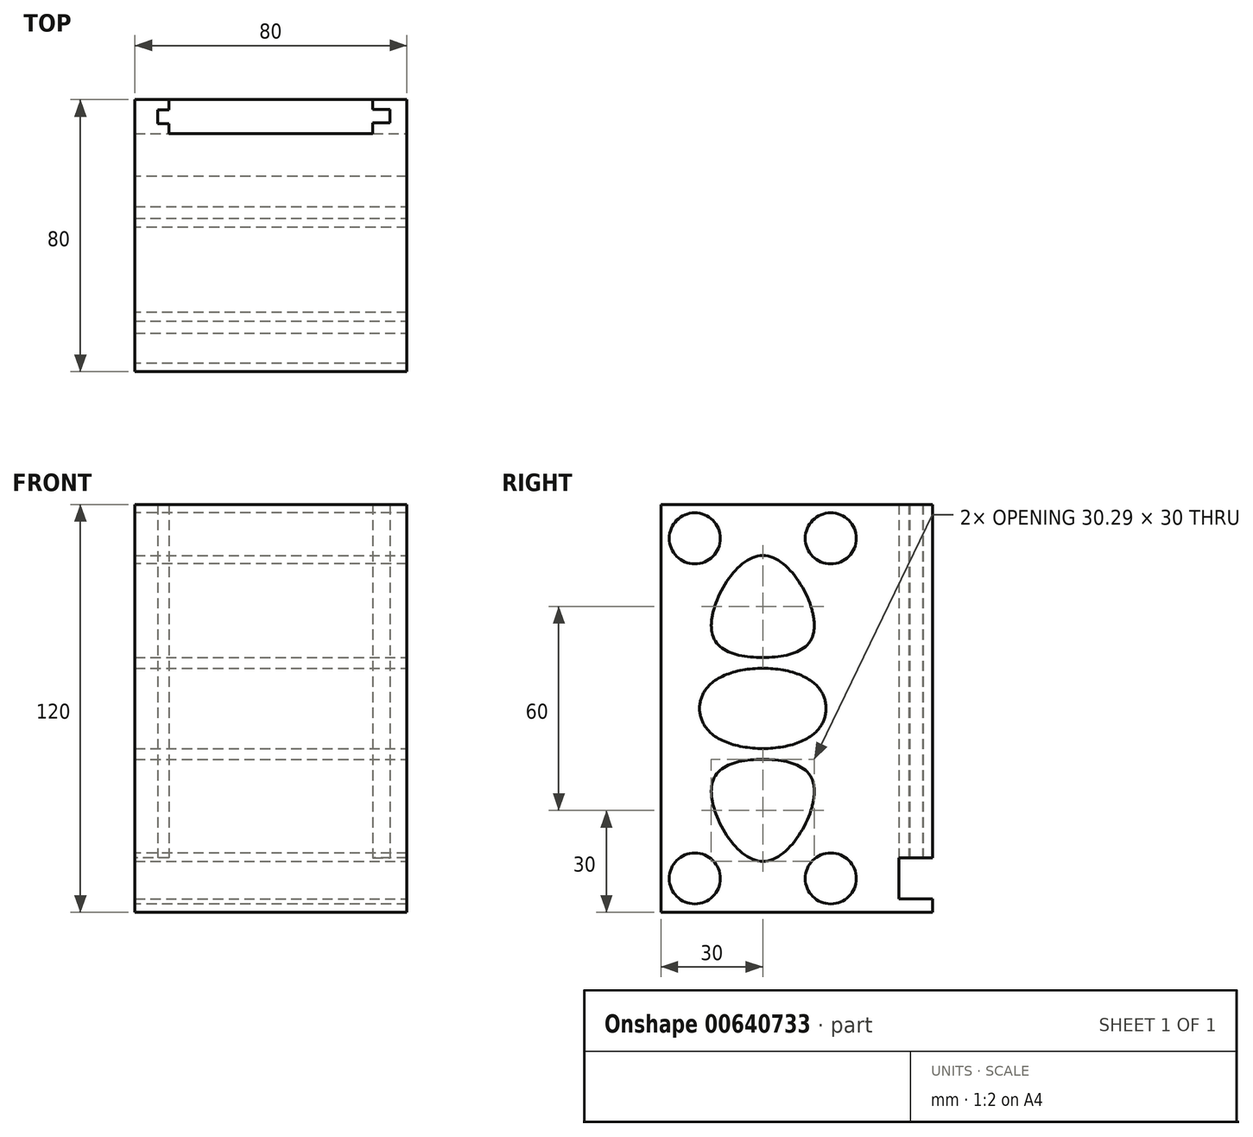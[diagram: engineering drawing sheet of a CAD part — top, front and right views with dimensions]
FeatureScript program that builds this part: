
annotation { "Feature Type Name" : "Feature", "Feature Type Description" : "" }
export const myFeature = defineFeature(function(context is Context, id is Id, definition is map)
    precondition{}
    {
        {
            var Q0;
            Q0=qCreatedBy(makeId("Top.planeOp"),FACE);
            var sketch = newSketch(context, id + "F0", { "sketchPlane" : qUnion([Q0])});
            skLineSegment(sketch, "E0.bottom", {"start": v(-25, 10) * mm, "end": v(25, 10) * mm});
            skLineSegment(sketch, "E0.top", {"start": v(-25, -10) * mm, "end": v(25, -10) * mm});
            skLineSegment(sketch, "E0.left", {"start": v(-25, 10) * mm, "end": v(-25, -10) * mm});
            skLineSegment(sketch, "E0.right", {"start": v(25, 10) * mm, "end": v(25, -10) * mm});
            skPoint(sketch, "E0.middle", {"position": v(0, 0) * mm});
            skPoint(sketch, "E1.middle", {"position": v(-25, 10) * mm});
            skPoint(sketch, "E2.middle", {"position": v(25, 10) * mm});
            skPoint(sketch, "E3.middle", {"position": v(25, -10) * mm});
            skLineSegment(sketch, "E4.bottom", {"start": v(-50, 0) * mm, "end": v(0, 0) * mm});
            skLineSegment(sketch, "E4.top", {"start": v(-50, -20) * mm, "end": v(0, -20) * mm});
            skLineSegment(sketch, "E4.left", {"start": v(-50, 0) * mm, "end": v(-50, -20) * mm});
            skLineSegment(sketch, "E4.right", {"start": v(0, 0) * mm, "end": v(0, -20) * mm});
            skPoint(sketch, "E4.middle", {"position": v(-25, -10) * mm});
            skLineSegment(sketch, "E5.bottom", {"start": v(0, 0) * mm, "end": v(50, 0) * mm});
            skLineSegment(sketch, "E5.top", {"start": v(0, -20) * mm, "end": v(50, -20) * mm});
            skLineSegment(sketch, "E5.right", {"start": v(50, 0) * mm, "end": v(50, -20) * mm});
            skLineSegment(sketch, "E6.bottom", {"start": v(50, 0) * mm, "end": v(0, 0) * mm});
            skLineSegment(sketch, "E6.top", {"start": v(50, 20) * mm, "end": v(0, 20) * mm});
            skLineSegment(sketch, "E6.left", {"start": v(50, 0) * mm, "end": v(50, 20) * mm});
            skLineSegment(sketch, "E6.right", {"start": v(0, 0) * mm, "end": v(0, 20) * mm});
            skLineSegment(sketch, "E7.top", {"start": v(-50, 20) * mm, "end": v(0, 20) * mm});
            skLineSegment(sketch, "E7.left", {"start": v(-50, 0) * mm, "end": v(-50, 20) * mm});
            skCircle(sketch, "E8", {"center": v(-50, 20) * mm, "radius": 10 * mm});
            skCircle(sketch, "E9", {"center": v(50, 20) * mm, "radius": 10 * mm});
            skCircle(sketch, "E10", {"center": v(50, -20) * mm, "radius": 10 * mm});
            skCircle(sketch, "E11", {"center": v(-50, -20) * mm, "radius": 10 * mm});
            skCircle(sketch, "E12", {"center": v(-50, 0) * mm, "radius": 10 * mm});
            skCircle(sketch, "E13", {"center": v(50, 0) * mm, "radius": 10 * mm});
            skLineSegment(sketch, "E14.bottom", {"start": v(-30, 30) * mm, "end": v(30, 30) * mm});
            skLineSegment(sketch, "E14.top", {"start": v(-30, 10) * mm, "end": v(30, 10) * mm});
            skLineSegment(sketch, "E14.left", {"start": v(-30, 30) * mm, "end": v(-30, 10) * mm});
            skLineSegment(sketch, "E14.right", {"start": v(30, 30) * mm, "end": v(30, 10) * mm});
            skPoint(sketch, "E14.middle", {"position": v(0, 20) * mm});
            skLineSegment(sketch, "E15", {"start": v(-30, 20) * mm, "end": v(-30, 10) * mm});
            skLineSegment(sketch, "E16.bottom", {"start": v(-33.31, 17) * mm, "end": v(-26.69, 17) * mm});
            skLineSegment(sketch, "E16.top", {"start": v(-33.31, 13) * mm, "end": v(-26.69, 13) * mm});
            skLineSegment(sketch, "E16.left", {"start": v(-33.31, 17) * mm, "end": v(-33.31, 13) * mm});
            skLineSegment(sketch, "E16.right", {"start": v(-26.69, 17) * mm, "end": v(-26.69, 13) * mm});
            skPoint(sketch, "E16.middle", {"position": v(-30, 15) * mm});
            skLineSegment(sketch, "E17.bottom", {"start": v(35, 17.2) * mm, "end": v(25, 17.2) * mm});
            skLineSegment(sketch, "E17.top", {"start": v(35, 13.2) * mm, "end": v(25, 13.2) * mm});
            skLineSegment(sketch, "E17.left", {"start": v(35, 17.2) * mm, "end": v(35, 13.2) * mm});
            skLineSegment(sketch, "E17.right", {"start": v(25, 17.2) * mm, "end": v(25, 13.2) * mm});
            skPoint(sketch, "E17.middle", {"position": v(30, 15.2) * mm});
            skFitSpline(sketch, "E18", {"points": [v(-40, -20) * mm, v(0, 0) * mm, v(40, -20) * mm], "startDerivative": vector(80, 60) * mm, "endDerivative": vector(80, -60) * mm});
            skSolve(sketch);
        }
        {
            var Q0;
            {var subQ0=sQuery(id+"F0.wireOp",EDGE,"E7.left");var subQ1=sQuery(id+"F0.wireOp",EDGE,"E7.top");var subQ2=makeQuery(id+"F0.imprint","INTERSECT",VERTEX,{"derivedFrom":[subQ1,subQ0]});Q0=makeQuery(id+"F0.imprint","IMPRINT",FACE,{"disambiguationData":[TD([[makeQuery(id+"F0.imprint","IMPRINT",EDGE,{"disambiguationData":[TD([[subQ2,-1.0]])],"derivedFrom":subQ1}),1.0]])]});}
            var Q1;
            {var subQ0=sQuery(id+"F0.wireOp",EDGE,"E7.left");var subQ1=sQuery(id+"F0.wireOp",EDGE,"E7.top");var subQ2=makeQuery(id+"F0.imprint","INTERSECT",VERTEX,{"derivedFrom":[subQ1,subQ0]});Q1=makeQuery(id+"F0.imprint","IMPRINT",FACE,{"disambiguationData":[TD([[makeQuery(id+"F0.imprint","IMPRINT",EDGE,{"disambiguationData":[TD([[subQ2,-1.0]])],"derivedFrom":subQ1}),-1.0]])]});}
            var Q2;
            {var subQ0=sQuery(id+"F0.wireOp",EDGE,"E16.left");Q2=makeQuery(id+"F0.imprint","IMPRINT",FACE,{"disambiguationData":[TD([[makeQuery(id+"F0.imprint","IMPRINT",EDGE,{"derivedFrom":subQ0}),-1.0]])]});}
            var Q3;
            {var subQ0=sQuery(id+"F0.wireOp",EDGE,"E14.top");var subQ1=sQuery(id+"F0.wireOp",EDGE,"E0.left");var subQ2=makeQuery(id+"F0.imprint","INTERSECT",VERTEX,{"derivedFrom":[subQ1,subQ0]});Q3=makeQuery(id+"F0.imprint","IMPRINT",FACE,{"disambiguationData":[TD([[makeQuery(id+"F0.imprint","IMPRINT",EDGE,{"disambiguationData":[TD([[subQ2,-1.0]])],"derivedFrom":subQ1}),1.0]])]});}
            var Q4;
            {var subQ0=sQuery(id+"F0.wireOp",EDGE,"E14.top");var subQ1=sQuery(id+"F0.wireOp",EDGE,"E0.right");var subQ2=makeQuery(id+"F0.imprint","INTERSECT",VERTEX,{"derivedFrom":[subQ1,subQ0]});Q4=makeQuery(id+"F0.imprint","IMPRINT",FACE,{"disambiguationData":[TD([[makeQuery(id+"F0.imprint","IMPRINT",EDGE,{"disambiguationData":[TD([[subQ2,-1.0]])],"derivedFrom":subQ1}),-1.0]])]});}
            var Q5;
            {var subQ0=sQuery(id+"F0.wireOp",EDGE,"E6.bottom");var subQ1=sQuery(id+"F0.wireOp",EDGE,"E0.right");var subQ2=makeQuery(id+"F0.imprint","INTERSECT",VERTEX,{"derivedFrom":[subQ1,subQ0]});Q5=makeQuery(id+"F0.imprint","IMPRINT",FACE,{"disambiguationData":[TD([[makeQuery(id+"F0.imprint","IMPRINT",EDGE,{"disambiguationData":[TD([[subQ2,-1.0]])],"derivedFrom":subQ1}),-1.0]])]});}
            var Q6;
            {var subQ0=sQuery(id+"F0.wireOp",EDGE,"E4.bottom");var subQ1=sQuery(id+"F0.wireOp",EDGE,"E0.left");var subQ2=makeQuery(id+"F0.imprint","INTERSECT",VERTEX,{"derivedFrom":[subQ1,subQ0]});Q6=makeQuery(id+"F0.imprint","IMPRINT",FACE,{"disambiguationData":[TD([[makeQuery(id+"F0.imprint","IMPRINT",EDGE,{"disambiguationData":[TD([[subQ2,-1.0]])],"derivedFrom":subQ1}),1.0]])]});}
            var Q7;
            {var subQ1=sQuery(id+"F0.wireOp",EDGE,"E4.bottom");var subQ7=sQuery(id+"F0.wireOp",EDGE,"E0.left");var subQ9=makeQuery(id+"F0.imprint","INTERSECT",VERTEX,{"derivedFrom":[subQ7,subQ1]});Q7=makeQuery(id+"F0.imprint","IMPRINT",FACE,{"disambiguationData":[TD([[makeQuery(id+"F0.imprint","IMPRINT",EDGE,{"disambiguationData":[TD([[subQ9,-1.0]])],"derivedFrom":subQ7}),-1.0]])]});}
            var Q8;
            {var subQ0=sQuery(id+"F0.wireOp",EDGE,"E4.left");var subQ1=sQuery(id+"F0.wireOp",EDGE,"E4.top");var subQ2=makeQuery(id+"F0.imprint","INTERSECT",VERTEX,{"derivedFrom":[subQ1,subQ0]});Q8=makeQuery(id+"F0.imprint","IMPRINT",FACE,{"disambiguationData":[TD([[makeQuery(id+"F0.imprint","IMPRINT",EDGE,{"disambiguationData":[TD([[subQ2,-1.0]])],"derivedFrom":subQ1}),1.0]])]});}
            var Q9;
            {var subQ0=sQuery(id+"F0.wireOp",EDGE,"E4.left");var subQ1=sQuery(id+"F0.wireOp",EDGE,"E4.top");var subQ2=makeQuery(id+"F0.imprint","INTERSECT",VERTEX,{"derivedFrom":[subQ1,subQ0]});Q9=makeQuery(id+"F0.imprint","IMPRINT",FACE,{"disambiguationData":[TD([[makeQuery(id+"F0.imprint","IMPRINT",EDGE,{"disambiguationData":[TD([[subQ2,-1.0]])],"derivedFrom":subQ1}),-1.0]])]});}
            var Q10;
            {var subQ11=sQuery(id+"F0.wireOp",EDGE,"E17.left");Q10=makeQuery(id+"F0.imprint","IMPRINT",FACE,{"disambiguationData":[TD([[makeQuery(id+"F0.imprint","IMPRINT",EDGE,{"derivedFrom":subQ11}),1.0]])]});}
            var Q11;
            {var subQ0=sQuery(id+"F0.wireOp",EDGE,"E6.left");var subQ1=sQuery(id+"F0.wireOp",EDGE,"E6.top");var subQ2=makeQuery(id+"F0.imprint","INTERSECT",VERTEX,{"derivedFrom":[subQ1,subQ0]});Q11=makeQuery(id+"F0.imprint","IMPRINT",FACE,{"disambiguationData":[TD([[makeQuery(id+"F0.imprint","IMPRINT",EDGE,{"disambiguationData":[TD([[subQ2,-1.0]])],"derivedFrom":subQ1}),1.0]])]});}
            var Q12;
            {var subQ0=sQuery(id+"F0.wireOp",EDGE,"E6.left");var subQ1=sQuery(id+"F0.wireOp",EDGE,"E6.top");var subQ2=makeQuery(id+"F0.imprint","INTERSECT",VERTEX,{"derivedFrom":[subQ1,subQ0]});Q12=makeQuery(id+"F0.imprint","IMPRINT",FACE,{"disambiguationData":[TD([[makeQuery(id+"F0.imprint","IMPRINT",EDGE,{"disambiguationData":[TD([[subQ2,-1.0]])],"derivedFrom":subQ1}),-1.0]])]});}
            var Q13;
            {var subQ1=sQuery(id+"F0.wireOp",EDGE,"E6.bottom");var subQ7=sQuery(id+"F0.wireOp",EDGE,"E0.right");var subQ8=makeQuery(id+"F0.imprint","INTERSECT",VERTEX,{"derivedFrom":[subQ7,subQ1]});Q13=makeQuery(id+"F0.imprint","IMPRINT",FACE,{"disambiguationData":[TD([[makeQuery(id+"F0.imprint","IMPRINT",EDGE,{"disambiguationData":[TD([[subQ8,-1.0]])],"derivedFrom":subQ7}),1.0]])]});}
            var Q14;
            {var subQ0=sQuery(id+"F0.wireOp",EDGE,"E5.right");var subQ1=sQuery(id+"F0.wireOp",EDGE,"E5.top");var subQ2=makeQuery(id+"F0.imprint","INTERSECT",VERTEX,{"derivedFrom":[subQ1,subQ0]});Q14=makeQuery(id+"F0.imprint","IMPRINT",FACE,{"disambiguationData":[TD([[makeQuery(id+"F0.imprint","IMPRINT",EDGE,{"disambiguationData":[TD([[subQ2,1.0]])],"derivedFrom":subQ1}),1.0]])]});}
            var Q15;
            {var subQ0=sQuery(id+"F0.wireOp",EDGE,"E5.right");var subQ1=sQuery(id+"F0.wireOp",EDGE,"E5.top");var subQ2=makeQuery(id+"F0.imprint","INTERSECT",VERTEX,{"derivedFrom":[subQ1,subQ0]});Q15=makeQuery(id+"F0.imprint","IMPRINT",FACE,{"disambiguationData":[TD([[makeQuery(id+"F0.imprint","IMPRINT",EDGE,{"disambiguationData":[TD([[subQ2,1.0]])],"derivedFrom":subQ1}),-1.0]])]});}
            var Q16;
            {var subQ3=sQuery(id+"F0.wireOp",EDGE,"E0.top");var subQ7=sQuery(id+"F0.wireOp",EDGE,"E0.right");var subQ8=makeQuery(id+"F0.imprint","INTERSECT",VERTEX,{"derivedFrom":[subQ3,subQ7]});Q16=makeQuery(id+"F0.imprint","IMPRINT",FACE,{"disambiguationData":[TD([[makeQuery(id+"F0.imprint","IMPRINT",EDGE,{"disambiguationData":[TD([[subQ8,1.0]])],"derivedFrom":subQ3}),-1.0]])]});}
            var Q17;
            {var subQ5=sQuery(id+"F0.wireOp",EDGE,"E0.left");var subQ7=sQuery(id+"F0.wireOp",EDGE,"E0.top");var subQ8=makeQuery(id+"F0.imprint","INTERSECT",VERTEX,{"derivedFrom":[subQ7,subQ5]});Q17=makeQuery(id+"F0.imprint","IMPRINT",FACE,{"disambiguationData":[TD([[makeQuery(id+"F0.imprint","IMPRINT",EDGE,{"disambiguationData":[TD([[subQ8,-1.0]])],"derivedFrom":subQ7}),-1.0]])]});}
            var Q18;
            {var subQ0=sQuery(id+"F0.wireOp",EDGE,"E0.left");var subQ1=sQuery(id+"F0.wireOp",EDGE,"E0.top");var subQ2=makeQuery(id+"F0.imprint","INTERSECT",VERTEX,{"derivedFrom":[subQ1,subQ0]});Q18=makeQuery(id+"F0.imprint","IMPRINT",FACE,{"disambiguationData":[TD([[makeQuery(id+"F0.imprint","IMPRINT",EDGE,{"disambiguationData":[TD([[subQ2,-1.0]])],"derivedFrom":subQ1}),1.0]])]});}
            var Q19;
            {var subQ0=sQuery(id+"F0.wireOp",EDGE,"E0.right");var subQ1=sQuery(id+"F0.wireOp",EDGE,"E0.top");var subQ2=makeQuery(id+"F0.imprint","INTERSECT",VERTEX,{"derivedFrom":[subQ1,subQ0]});Q19=makeQuery(id+"F0.imprint","IMPRINT",FACE,{"disambiguationData":[TD([[makeQuery(id+"F0.imprint","IMPRINT",EDGE,{"disambiguationData":[TD([[subQ2,1.0]])],"derivedFrom":subQ1}),1.0]])]});}
            extrude(context, id + "F1", {"entities" : qUnion([Q0, Q1, Q2, Q3, Q4, Q5, Q6, Q7, Q8, Q9, Q10, Q11, Q12, Q13, Q14, Q15, Q16, Q17, Q18, Q19]), "depth" : 120 * mm, "offsetDistance" : 25 * mm});
        }
        {
            var Q0;
            {var subQ6=sQuery(id+"F0.wireOp",EDGE,"E16.right");Q0=makeQuery(id+"F0.imprint","IMPRINT",FACE,{"disambiguationData":[TD([[makeQuery(id+"F0.imprint","IMPRINT",EDGE,{"derivedFrom":subQ6}),1.0]])]});}
            var Q1;
            {var subQ5=sQuery(id+"F0.wireOp",EDGE,"E16.right");Q1=makeQuery(id+"F0.imprint","IMPRINT",FACE,{"disambiguationData":[TD([[makeQuery(id+"F0.imprint","IMPRINT",EDGE,{"derivedFrom":subQ5}),-1.0]])]});}
            var Q2;
            {var subQ5=sQuery(id+"F0.wireOp",EDGE,"E16.left");Q2=makeQuery(id+"F0.imprint","IMPRINT",FACE,{"disambiguationData":[TD([[makeQuery(id+"F0.imprint","IMPRINT",EDGE,{"derivedFrom":subQ5}),1.0]])]});}
            var Q3;
            {var subQ5=sQuery(id+"F0.wireOp",EDGE,"E17.left");Q3=makeQuery(id+"F0.imprint","IMPRINT",FACE,{"disambiguationData":[TD([[makeQuery(id+"F0.imprint","IMPRINT",EDGE,{"derivedFrom":subQ5}),-1.0]])]});}
            var Q4;
            {var subQ5=sQuery(id+"F0.wireOp",EDGE,"E17.right");Q4=makeQuery(id+"F0.imprint","IMPRINT",FACE,{"disambiguationData":[TD([[makeQuery(id+"F0.imprint","IMPRINT",EDGE,{"derivedFrom":subQ5}),1.0]])]});}
            var Q5;
            {var subQ13=sQuery(id+"F0.wireOp",EDGE,"E17.right");Q5=makeQuery(id+"F0.imprint","IMPRINT",FACE,{"disambiguationData":[TD([[makeQuery(id+"F0.imprint","IMPRINT",EDGE,{"derivedFrom":subQ13}),-1.0]])]});}
            extrude(context, id + "F2", {"entities" : qUnion([Q0, Q1, Q2, Q3, Q4, Q5]), "operationType" : NewBodyOperationType.ADD, "depth" : 4 * mm, "offsetDistance" : 25 * mm});
        }
        {
            var Q0;
            Q0=qCreatedBy(makeId("Right.planeOp"),FACE);
            var sketch = newSketch(context, id + "F3", { "sketchPlane" : qUnion([Q0])});
            skLineSegment(sketch, "E19", {"start": v(0, 0) * mm, "end": v(15, 0) * mm});
            skLineSegment(sketch, "E20", {"start": v(15, 0) * mm, "end": v(15, 10) * mm});
            skLineSegment(sketch, "E21.bottom", {"start": v(20, 16) * mm, "end": v(10, 16) * mm});
            skLineSegment(sketch, "E21.top", {"start": v(20, 4) * mm, "end": v(10, 4) * mm});
            skLineSegment(sketch, "E21.right", {"start": v(10, 16) * mm, "end": v(10, 4) * mm});
            skPoint(sketch, "E21.middle", {"position": v(15, 10) * mm});
            skLineSegment(sketch, "E22", {"start": v(20, 16) * mm, "end": v(30, 16) * mm});
            skLineSegment(sketch, "E23", {"start": v(20, 4) * mm, "end": v(30, 4) * mm});
            skLineSegment(sketch, "E24", {"start": v(30, 16) * mm, "end": v(30, 4) * mm});
            skSolve(sketch);
        }
        {
            var Q0;
            Q0=makeQuery(id+"F3.imprint","IMPRINT",FACE,{"disambiguationData":[TD([[makeQuery(id+"F3.imprint","IMPRINT",EDGE,{"derivedFrom":sQuery(id+"F3.wireOp",EDGE,"E21.bottom")}),1.0]])]});
            extrude(context, id + "F4", {"entities" : qUnion([Q0]), "operationType" : NewBodyOperationType.REMOVE, "depth" : 100 * mm, "offsetDistance" : 25 * mm, "hasSecondDirection" : true, "secondDirectionOppositeDirection" : true, "secondDirectionDepth" : 100 * mm});
        }
        {
            var Q0;
            Q0=qCreatedBy(makeId("Top.planeOp"),FACE);
            var sketch = newSketch(context, id + "F5", { "sketchPlane" : qUnion([Q0])});
            skLineSegment(sketch, "E25", {"start": v(0, 0) * mm, "end": v(-50, 0) * mm});
            skLineSegment(sketch, "E26", {"start": v(0, 0) * mm, "end": v(50, 0) * mm});
            skLineSegment(sketch, "E27.bottom", {"start": v(-60, -41.73) * mm, "end": v(-40, -41.73) * mm});
            skLineSegment(sketch, "E27.top", {"start": v(-60, 41.73) * mm, "end": v(-40, 41.73) * mm});
            skLineSegment(sketch, "E27.left", {"start": v(-60, -41.73) * mm, "end": v(-60, 41.73) * mm});
            skLineSegment(sketch, "E27.right", {"start": v(-40, -41.73) * mm, "end": v(-40, 41.73) * mm});
            skPoint(sketch, "E27.middle", {"position": v(-50, 0) * mm});
            skLineSegment(sketch, "E28.bottom", {"start": v(40, -36.42) * mm, "end": v(60, -36.42) * mm});
            skLineSegment(sketch, "E28.top", {"start": v(40, 36.42) * mm, "end": v(60, 36.42) * mm});
            skLineSegment(sketch, "E28.left", {"start": v(40, -36.42) * mm, "end": v(40, 36.42) * mm});
            skLineSegment(sketch, "E28.right", {"start": v(60, -36.42) * mm, "end": v(60, 36.42) * mm});
            skPoint(sketch, "E28.middle", {"position": v(50, 0) * mm});
            skSolve(sketch);
        }
        {
            var Q0;
            {var subQ1=sQuery(id+"F5.wireOp",EDGE,"E27.bottom");Q0=makeQuery(id+"F5.imprint","IMPRINT",FACE,{"disambiguationData":[TD([[makeQuery(id+"F5.imprint","IMPRINT",EDGE,{"derivedFrom":subQ1}),1.0]])]});}
            var Q1;
            {var subQ3=sQuery(id+"F5.wireOp",EDGE,"E28.bottom");Q1=makeQuery(id+"F5.imprint","IMPRINT",FACE,{"disambiguationData":[TD([[makeQuery(id+"F5.imprint","IMPRINT",EDGE,{"derivedFrom":subQ3}),1.0]])]});}
            extrude(context, id + "F6", {"entities" : qUnion([Q0, Q1]), "operationType" : NewBodyOperationType.REMOVE, "depth" : 120 * mm, "offsetDistance" : 25 * mm});
        }
        {
            var Q0;
            Q0=makeQuery(id+"F1.opExtrude","SWEPT_FACE",FACE,{"disambiguationData":[OSD([sQuery(id+"F0.wireOp",EDGE,"E4.top"),sQuery(id+"F0.wireOp",EDGE,"E5.top")])]});
            extrude(context, id + "F7", {"entities" : qUnion([Q0]), "operationType" : NewBodyOperationType.ADD, "depth" : 40 * mm, "offsetDistance" : 25 * mm});
        }
        {
            var Q0;
            Q0=qCreatedBy(makeId("Right.planeOp"),FACE);
            var sketch = newSketch(context, id + "F8", { "sketchPlane" : qUnion([Q0])});
            skLineSegment(sketch, "E29.bottom", {"start": v(0, 0) * mm, "end": v(-60, 0) * mm});
            skLineSegment(sketch, "E29.top", {"start": v(0, 120) * mm, "end": v(-60, 120) * mm});
            skLineSegment(sketch, "E29.left", {"start": v(0, 0) * mm, "end": v(0, 60) * mm});
            skLineSegment(sketch, "E29.right", {"start": v(-60, 0) * mm, "end": v(-60, 120) * mm});
            skLineSegment(sketch, "E30", {"start": v(-10, 60) * mm, "end": v(-30, 60) * mm});
            skLineSegment(sketch, "E31", {"start": v(-30, 110) * mm, "end": v(-30, 120) * mm});
            skLineSegment(sketch, "E32.bottom", {"start": v(-30, 110) * mm, "end": v(-42.5, 110) * mm});
            skLineSegment(sketch, "E32.top", {"start": v(-10, 10) * mm, "end": v(-50, 10) * mm});
            skLineSegment(sketch, "E32.left", {"start": v(-10, 110) * mm, "end": v(-10, 17.5) * mm});
            skLineSegment(sketch, "E32.right", {"start": v(-50, 110) * mm, "end": v(-50, 17.5) * mm});
            skPoint(sketch, "E32.middle", {"position": v(-30, 60) * mm});
            skCircle(sketch, "E33", {"center": v(-10, 110) * mm, "radius": 7.5 * mm});
            skCircle(sketch, "E34", {"center": v(-50, 110) * mm, "radius": 7.5 * mm});
            skCircle(sketch, "E35", {"center": v(-50, 10) * mm, "radius": 7.5 * mm});
            skCircle(sketch, "E36", {"center": v(-10, 10) * mm, "radius": 7.5 * mm});
            skPoint(sketch, "E37.start.orphan", {"position": v(-30, 0) * mm});
            skPoint(sketch, "E38.orphan", {"position": v(0, 60) * mm});
            skPoint(sketch, "E39.trimOffspring.end.orphan", {"position": v(-60, 60) * mm});
            skSolve(sketch);
        }
        {
            var Q0;
            Q0 = qSketchRegion(id + "F8", true);
            extrude(context, id + "F9", {"entities" : qUnion([Q0]), "operationType" : NewBodyOperationType.REMOVE, "depth" : 100 * mm, "offsetDistance" : 25 * mm, "hasSecondDirection" : true, "secondDirectionOppositeDirection" : true, "secondDirectionDepth" : 100 * mm});
        }
        {
            var Q0;
            Q0=qCreatedBy(makeId("Right.planeOp"),FACE);
            cPlane(context, id + "F10", {"entities" : qUnion([Q0]), "cplaneType" : CPlaneType.OFFSET, "offset" : 40 * mm, "width" : 150 * mm, "height" : 150 * mm});
        }
        {
            var Q0;
            Q0=qCreatedBy(id+"F10.planeOp",FACE);
            var sketch = newSketch(context, id + "F11", { "sketchPlane" : qUnion([Q0])});
            skLineSegment(sketch, "E40", {"start": v(0, 0) * mm, "end": v(0, 120) * mm});
            skLineSegment(sketch, "E41", {"start": v(0, 60) * mm, "end": v(-60, 60) * mm});
            skLineSegment(sketch, "E42", {"start": v(-60, 60) * mm, "end": v(-60, 120) * mm});
            skLineSegment(sketch, "E43", {"start": v(-60, 60) * mm, "end": v(-60, 0) * mm});
            skLineSegment(sketch, "E44", {"start": v(-60, 90) * mm, "end": v(0, 90) * mm});
            skLineSegment(sketch, "E45", {"start": v(-60, 30) * mm, "end": v(0, 30) * mm});
            skLineSegment(sketch, "E46", {"start": v(-30, 30) * mm, "end": v(-30, 60) * mm});
            skLineSegment(sketch, "E47", {"start": v(-30, 60) * mm, "end": v(-30, 90) * mm});
            skLineSegment(sketch, "E48", {"start": v(-60, 120) * mm, "end": v(-60, 90) * mm});
            skLineSegment(sketch, "E49", {"start": v(-60, 90) * mm, "end": v(-60, 60) * mm});
            skLineSegment(sketch, "E50", {"start": v(-60, 60) * mm, "end": v(-60, 30) * mm});
            skLineSegment(sketch, "E51", {"start": v(-60, 30) * mm, "end": v(-60, 0) * mm});
            skLineSegment(sketch, "E52", {"start": v(-60, 75) * mm, "end": v(0, 75) * mm});
            skLineSegment(sketch, "E53", {"start": v(0, 75) * mm, "end": v(-30, 60) * mm});
            skLineSegment(sketch, "E54", {"start": v(-60, 75) * mm, "end": v(-30, 60) * mm});
            skLineSegment(sketch, "E55", {"start": v(-60, 45) * mm, "end": v(0, 45) * mm});
            skLineSegment(sketch, "E56", {"start": v(0, 45) * mm, "end": v(-30, 60) * mm});
            skLineSegment(sketch, "E57", {"start": v(-60, 45) * mm, "end": v(-30, 60) * mm});
            skLineSegment(sketch, "E58", {"start": v(-60, 45) * mm, "end": v(-30, 30) * mm});
            skLineSegment(sketch, "E59", {"start": v(0, 45) * mm, "end": v(-30, 30) * mm});
            skLineSegment(sketch, "E60", {"start": v(-60, 75) * mm, "end": v(-30, 90) * mm});
            skLineSegment(sketch, "E61", {"start": v(0, 75) * mm, "end": v(-30, 90) * mm});
            skLineSegment(sketch, "E62", {"start": v(-60, 120) * mm, "end": v(0, 120) * mm});
            skLineSegment(sketch, "E63", {"start": v(-60, 90) * mm, "end": v(-30, 120) * mm});
            skLineSegment(sketch, "E64", {"start": v(-30, 120) * mm, "end": v(0, 90) * mm});
            skLineSegment(sketch, "E65", {"start": v(-60, 0) * mm, "end": v(0, 0) * mm});
            skLineSegment(sketch, "E66", {"start": v(-60, 30) * mm, "end": v(-30, 0) * mm});
            skLineSegment(sketch, "E67", {"start": v(-30, 0) * mm, "end": v(0, 30) * mm});
            skLineSegment(sketch, "E68", {"start": v(-30, 30) * mm, "end": v(-30, 0) * mm});
            skLineSegment(sketch, "E69", {"start": v(-30, 90) * mm, "end": v(-30, 120) * mm});
            skLineSegment(sketch, "E70", {"start": v(-162.58, 48.52) * mm, "end": v(-145.65, 65.46) * mm});
            skFitSpline(sketch, "E71", {"points": [v(-45, 37.5) * mm, v(-30, 15) * mm, v(-15, 37.5) * mm, v(-30, 45) * mm, v(-45, 37.5) * mm]});
            skFitSpline(sketch, "E72", {"points": [v(-45, 82.5) * mm, v(-30, 105) * mm, v(-15, 82.5) * mm, v(-30, 75) * mm, v(-45, 82.5) * mm]});
            skFitSpline(sketch, "E73", {"points": [v(-15, 52.5) * mm, v(-15, 67.5) * mm, v(-45, 67.5) * mm, v(-45, 52.5) * mm, v(-15, 52.5) * mm]});
            skSolve(sketch);
        }
        {
            var Q0;
            {var subQ1=sQuery(id+"F11.wireOp",EDGE,"E44");var subQ3=sQuery(id+"F11.wireOp",EDGE,"E72");var subQ4=makeQuery(id+"F11.imprint","INTERSECT",VERTEX,{"disambiguationData":[OD(0.0)],"derivedFrom":[subQ1,subQ3]});Q0=makeQuery(id+"F11.imprint","IMPRINT",FACE,{"disambiguationData":[TD([[makeQuery(id+"F11.imprint","IMPRINT",EDGE,{"disambiguationData":[TD([[subQ4,-1.0]])],"derivedFrom":subQ3}),-1.0]])]});}
            var Q1;
            {var subQ1=sQuery(id+"F11.wireOp",EDGE,"E44");var subQ3=sQuery(id+"F11.wireOp",EDGE,"E72");var subQ4=makeQuery(id+"F11.imprint","INTERSECT",VERTEX,{"disambiguationData":[OD(0.0)],"derivedFrom":[subQ1,subQ3]});Q1=makeQuery(id+"F11.imprint","IMPRINT",FACE,{"disambiguationData":[TD([[makeQuery(id+"F11.imprint","IMPRINT",EDGE,{"disambiguationData":[TD([[subQ4,1.0]])],"derivedFrom":subQ3}),-1.0]])]});}
            var Q2;
            {var subQ0=sQuery(id+"F11.wireOp",EDGE,"E60");var subQ3=sQuery(id+"F11.wireOp",EDGE,"E72");var subQ5=makeQuery(id+"F11.imprint","INTERSECT",VERTEX,{"derivedFrom":[subQ0,subQ3]});Q2=makeQuery(id+"F11.imprint","IMPRINT",FACE,{"disambiguationData":[TD([[makeQuery(id+"F11.imprint","IMPRINT",EDGE,{"disambiguationData":[TD([[subQ5,1.0]])],"derivedFrom":subQ3}),-1.0]])]});}
            var Q3;
            {var subQ0=sQuery(id+"F11.wireOp",EDGE,"E61");var subQ3=sQuery(id+"F11.wireOp",EDGE,"E72");var subQ5=makeQuery(id+"F11.imprint","INTERSECT",VERTEX,{"derivedFrom":[subQ0,subQ3]});Q3=makeQuery(id+"F11.imprint","IMPRINT",FACE,{"disambiguationData":[TD([[makeQuery(id+"F11.imprint","IMPRINT",EDGE,{"disambiguationData":[TD([[subQ5,-1.0]])],"derivedFrom":subQ3}),-1.0]])]});}
            var Q4;
            {var subQ1=sQuery(id+"F11.wireOp",EDGE,"E44");var subQ3=sQuery(id+"F11.wireOp",EDGE,"E72");var subQ4=makeQuery(id+"F11.imprint","INTERSECT",VERTEX,{"disambiguationData":[OD(1.0)],"derivedFrom":[subQ1,subQ3]});Q4=makeQuery(id+"F11.imprint","IMPRINT",FACE,{"disambiguationData":[TD([[makeQuery(id+"F11.imprint","IMPRINT",EDGE,{"disambiguationData":[TD([[subQ4,-1.0]])],"derivedFrom":subQ3}),-1.0]])]});}
            var Q5;
            {var subQ1=sQuery(id+"F11.wireOp",EDGE,"E44");var subQ3=sQuery(id+"F11.wireOp",EDGE,"E72");var subQ4=makeQuery(id+"F11.imprint","INTERSECT",VERTEX,{"disambiguationData":[OD(1.0)],"derivedFrom":[subQ1,subQ3]});Q5=makeQuery(id+"F11.imprint","IMPRINT",FACE,{"disambiguationData":[TD([[makeQuery(id+"F11.imprint","IMPRINT",EDGE,{"disambiguationData":[TD([[subQ4,1.0]])],"derivedFrom":subQ3}),-1.0]])]});}
            var Q6;
            {var subQ1=sQuery(id+"F11.wireOp",EDGE,"E47");var subQ3=sQuery(id+"F11.wireOp",EDGE,"E73");var subQ4=makeQuery(id+"F11.imprint","INTERSECT",VERTEX,{"derivedFrom":[subQ1,subQ3]});Q6=makeQuery(id+"F11.imprint","IMPRINT",FACE,{"disambiguationData":[TD([[makeQuery(id+"F11.imprint","IMPRINT",EDGE,{"disambiguationData":[TD([[subQ4,1.0]])],"derivedFrom":subQ3}),1.0]])]});}
            var Q7;
            {var subQ1=sQuery(id+"F11.wireOp",EDGE,"E47");var subQ3=sQuery(id+"F11.wireOp",EDGE,"E73");var subQ4=makeQuery(id+"F11.imprint","INTERSECT",VERTEX,{"derivedFrom":[subQ1,subQ3]});Q7=makeQuery(id+"F11.imprint","IMPRINT",FACE,{"disambiguationData":[TD([[makeQuery(id+"F11.imprint","IMPRINT",EDGE,{"disambiguationData":[TD([[subQ4,-1.0]])],"derivedFrom":subQ3}),1.0]])]});}
            var Q8;
            {var subQ1=sQuery(id+"F11.wireOp",EDGE,"E41");var subQ3=sQuery(id+"F11.wireOp",EDGE,"E73");var subQ4=makeQuery(id+"F11.imprint","INTERSECT",VERTEX,{"disambiguationData":[OD(1.0)],"derivedFrom":[subQ1,subQ3]});Q8=makeQuery(id+"F11.imprint","IMPRINT",FACE,{"disambiguationData":[TD([[makeQuery(id+"F11.imprint","IMPRINT",EDGE,{"disambiguationData":[TD([[subQ4,1.0]])],"derivedFrom":subQ3}),1.0]])]});}
            var Q9;
            {var subQ1=sQuery(id+"F11.wireOp",EDGE,"E41");var subQ3=sQuery(id+"F11.wireOp",EDGE,"E73");var subQ4=makeQuery(id+"F11.imprint","INTERSECT",VERTEX,{"disambiguationData":[OD(1.0)],"derivedFrom":[subQ1,subQ3]});Q9=makeQuery(id+"F11.imprint","IMPRINT",FACE,{"disambiguationData":[TD([[makeQuery(id+"F11.imprint","IMPRINT",EDGE,{"disambiguationData":[TD([[subQ4,-1.0]])],"derivedFrom":subQ3}),1.0]])]});}
            var Q10;
            {var subQ1=sQuery(id+"F11.wireOp",EDGE,"E46");var subQ3=sQuery(id+"F11.wireOp",EDGE,"E73");var subQ4=makeQuery(id+"F11.imprint","INTERSECT",VERTEX,{"derivedFrom":[subQ1,subQ3]});Q10=makeQuery(id+"F11.imprint","IMPRINT",FACE,{"disambiguationData":[TD([[makeQuery(id+"F11.imprint","IMPRINT",EDGE,{"disambiguationData":[TD([[subQ4,1.0]])],"derivedFrom":subQ3}),1.0]])]});}
            var Q11;
            {var subQ1=sQuery(id+"F11.wireOp",EDGE,"E46");var subQ3=sQuery(id+"F11.wireOp",EDGE,"E73");var subQ4=makeQuery(id+"F11.imprint","INTERSECT",VERTEX,{"derivedFrom":[subQ1,subQ3]});Q11=makeQuery(id+"F11.imprint","IMPRINT",FACE,{"disambiguationData":[TD([[makeQuery(id+"F11.imprint","IMPRINT",EDGE,{"disambiguationData":[TD([[subQ4,-1.0]])],"derivedFrom":subQ3}),1.0]])]});}
            var Q12;
            {var subQ1=sQuery(id+"F11.wireOp",EDGE,"E41");var subQ3=sQuery(id+"F11.wireOp",EDGE,"E73");var subQ4=makeQuery(id+"F11.imprint","INTERSECT",VERTEX,{"disambiguationData":[OD(0.0)],"derivedFrom":[subQ1,subQ3]});Q12=makeQuery(id+"F11.imprint","IMPRINT",FACE,{"disambiguationData":[TD([[makeQuery(id+"F11.imprint","IMPRINT",EDGE,{"disambiguationData":[TD([[subQ4,1.0]])],"derivedFrom":subQ3}),1.0]])]});}
            var Q13;
            {var subQ1=sQuery(id+"F11.wireOp",EDGE,"E41");var subQ3=sQuery(id+"F11.wireOp",EDGE,"E73");var subQ4=makeQuery(id+"F11.imprint","INTERSECT",VERTEX,{"disambiguationData":[OD(0.0)],"derivedFrom":[subQ1,subQ3]});Q13=makeQuery(id+"F11.imprint","IMPRINT",FACE,{"disambiguationData":[TD([[makeQuery(id+"F11.imprint","IMPRINT",EDGE,{"disambiguationData":[TD([[subQ4,-1.0]])],"derivedFrom":subQ3}),1.0]])]});}
            var Q14;
            {var subQ0=sQuery(id+"F11.wireOp",EDGE,"E59");var subQ3=sQuery(id+"F11.wireOp",EDGE,"E71");var subQ5=makeQuery(id+"F11.imprint","INTERSECT",VERTEX,{"derivedFrom":[subQ0,subQ3]});Q14=makeQuery(id+"F11.imprint","IMPRINT",FACE,{"disambiguationData":[TD([[makeQuery(id+"F11.imprint","IMPRINT",EDGE,{"disambiguationData":[TD([[subQ5,-1.0]])],"derivedFrom":subQ3}),1.0]])]});}
            var Q15;
            {var subQ0=sQuery(id+"F11.wireOp",EDGE,"E58");var subQ3=sQuery(id+"F11.wireOp",EDGE,"E71");var subQ5=makeQuery(id+"F11.imprint","INTERSECT",VERTEX,{"derivedFrom":[subQ0,subQ3]});Q15=makeQuery(id+"F11.imprint","IMPRINT",FACE,{"disambiguationData":[TD([[makeQuery(id+"F11.imprint","IMPRINT",EDGE,{"disambiguationData":[TD([[subQ5,1.0]])],"derivedFrom":subQ3}),1.0]])]});}
            var Q16;
            {var subQ1=sQuery(id+"F11.wireOp",EDGE,"E45");var subQ3=sQuery(id+"F11.wireOp",EDGE,"E71");var subQ4=makeQuery(id+"F11.imprint","INTERSECT",VERTEX,{"disambiguationData":[OD(0.0)],"derivedFrom":[subQ1,subQ3]});Q16=makeQuery(id+"F11.imprint","IMPRINT",FACE,{"disambiguationData":[TD([[makeQuery(id+"F11.imprint","IMPRINT",EDGE,{"disambiguationData":[TD([[subQ4,1.0]])],"derivedFrom":subQ3}),1.0]])]});}
            var Q17;
            {var subQ1=sQuery(id+"F11.wireOp",EDGE,"E45");var subQ3=sQuery(id+"F11.wireOp",EDGE,"E71");var subQ4=makeQuery(id+"F11.imprint","INTERSECT",VERTEX,{"disambiguationData":[OD(0.0)],"derivedFrom":[subQ1,subQ3]});Q17=makeQuery(id+"F11.imprint","IMPRINT",FACE,{"disambiguationData":[TD([[makeQuery(id+"F11.imprint","IMPRINT",EDGE,{"disambiguationData":[TD([[subQ4,-1.0]])],"derivedFrom":subQ3}),1.0]])]});}
            var Q18;
            {var subQ1=sQuery(id+"F11.wireOp",EDGE,"E45");var subQ3=sQuery(id+"F11.wireOp",EDGE,"E71");var subQ4=makeQuery(id+"F11.imprint","INTERSECT",VERTEX,{"disambiguationData":[OD(1.0)],"derivedFrom":[subQ1,subQ3]});Q18=makeQuery(id+"F11.imprint","IMPRINT",FACE,{"disambiguationData":[TD([[makeQuery(id+"F11.imprint","IMPRINT",EDGE,{"disambiguationData":[TD([[subQ4,1.0]])],"derivedFrom":subQ3}),1.0]])]});}
            var Q19;
            {var subQ1=sQuery(id+"F11.wireOp",EDGE,"E45");var subQ3=sQuery(id+"F11.wireOp",EDGE,"E71");var subQ4=makeQuery(id+"F11.imprint","INTERSECT",VERTEX,{"disambiguationData":[OD(1.0)],"derivedFrom":[subQ1,subQ3]});Q19=makeQuery(id+"F11.imprint","IMPRINT",FACE,{"disambiguationData":[TD([[makeQuery(id+"F11.imprint","IMPRINT",EDGE,{"disambiguationData":[TD([[subQ4,-1.0]])],"derivedFrom":subQ3}),1.0]])]});}
            extrude(context, id + "F12", {"entities" : qUnion([Q0, Q1, Q2, Q3, Q4, Q5, Q6, Q7, Q8, Q9, Q10, Q11, Q12, Q13, Q14, Q15, Q16, Q17, Q18, Q19]), "operationType" : NewBodyOperationType.REMOVE, "oppositeDirection" : true, "depth" : 80 * mm, "offsetDistance" : 25 * mm});
        }
    });
